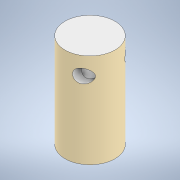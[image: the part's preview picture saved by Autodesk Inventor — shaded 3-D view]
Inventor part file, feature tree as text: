
AUTODESK INVENTOR PART (.ipt)
format: ipt  version: 2020 (Build 240168000, 168)  size: 145,920 bytes
history: native  units: mm
features: extrude x5, sketch x5, other x1, plane x1
ambient origin geometry x8: Origin, YZ Plane, XZ Plane, XY Plane, X Axis, Y Axis, Z Axis, Center Point
bodies: Body1 (feature_tree)
feature tree (12):
  other  "Sólido1"
  extrude  "Extrusión1"  Depth=146.5mm TaperAngle=0.0deg
  extrude  "Extrusión2"  Depth=6.0mm
  extrude  "Extrusión3"  Depth=3.75mm
  extrude  "Extrusión4"  Depth=22.0mm
  plane  "Plano de trabajo1"
  extrude  "Extrusión5"  Depth=41.5mm TaperAngle=0.0deg
  sketch  "Boceto1"  dims[d0=21.9mm d1=146.5mm d2=0.0mm]
  sketch  "Boceto2"  dims[d3=6.0mm d4=6.0mm]
  sketch  "Boceto4"  dims[d5=7.0mm d7=3.75mm]
  sketch  "Boceto5"  dims[d8=40.5mm d9=0.0mm d10=22.0mm]
  sketch  "Boceto6"  dims[d11=41.5mm d12=0.0mm d13=105.0mm d14=0.0mm d15=0.0mm d16=6.0mm d17=22.0mm d18=0.0mm]
